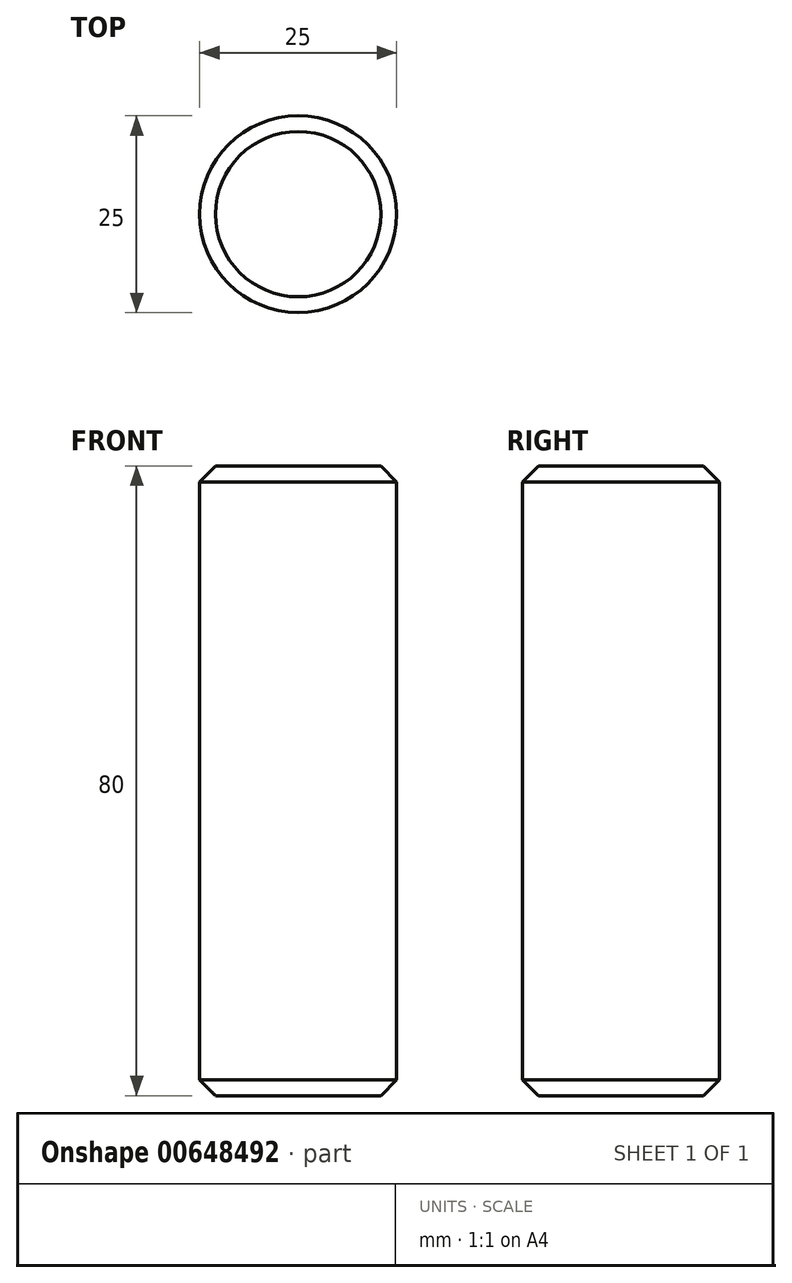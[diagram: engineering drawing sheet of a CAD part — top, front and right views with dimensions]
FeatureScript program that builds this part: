
annotation { "Feature Type Name" : "Feature", "Feature Type Description" : "" }
export const myFeature = defineFeature(function(context is Context, id is Id, definition is map)
    precondition{}
    {
        {
            var Q0;
            Q0=qCreatedBy(makeId("Front.planeOp"),FACE);
            var sketch = newSketch(context, id + "F0", { "sketchPlane" : qUnion([Q0])});
            skLineSegment(sketch, "E0.bottom", {"start": v(-12.5, 40) * mm, "end": v(0, 40) * mm});
            skLineSegment(sketch, "E0.top", {"start": v(-12.5, -40) * mm, "end": v(0, -40) * mm});
            skLineSegment(sketch, "E0.left", {"start": v(-12.5, 40) * mm, "end": v(-12.5, -40) * mm});
            skLineSegment(sketch, "E1", {"start": v(0, 52.22) * mm, "end": v(0, -40) * mm, "construction": true});
            skPoint(sketch, "E1.startSnap0", {"position": v(0, 40) * mm});
            skPoint(sketch, "E0.right.start.orphan", {"position": v(12.5, 40) * mm});
            skPoint(sketch, "E2.orphan", {"position": v(12.5, -40) * mm});
            skLineSegment(sketch, "E3.trimOffspring", {"start": v(0, 40) * mm, "end": v(0, -53.72) * mm, "construction": true});
            skLineSegment(sketch, "E4.trimOffspring", {"start": v(0, 40) * mm, "end": v(0, -40) * mm});
            skSolve(sketch);
        }
        {
            var Q0;
            Q0=makeQuery(id+"F0.imprint","IMPRINT",FACE,{"disambiguationData":[TD([[makeQuery(id+"F0.imprint","IMPRINT",EDGE,{"derivedFrom":sQuery(id+"F0.wireOp",EDGE,"E0.bottom")}),-1.0]])]});
            var Q1;
            Q1=sQuery(id+"F0.wireOp",EDGE,"E1");
            revolve(context, id + "F1", {"entities" : qUnion([Q0]), "axis" : qUnion([Q1]), "revolveType" : RevolveType.FULL});
        }
        {
            var Q0;
            Q0=makeQuery(id+"F1.opRevolve","SWEPT_EDGE",EDGE,{"disambiguationData":[OSD([sQuery(id+"F0.wireOp",EDGE,"E0.bottom"),sQuery(id+"F0.wireOp",EDGE,"E0.left")])]});
            var Q1;
            Q1=makeQuery(id+"F1.opRevolve","SWEPT_EDGE",EDGE,{"disambiguationData":[OSD([sQuery(id+"F0.wireOp",EDGE,"E0.top"),sQuery(id+"F0.wireOp",EDGE,"E0.left")])]});
            chamfer(context, id + "F2", {"entities" : qUnion([Q0, Q1]), "width" : 2 * mm, "tangentPropagation" : true});
        }
    });
